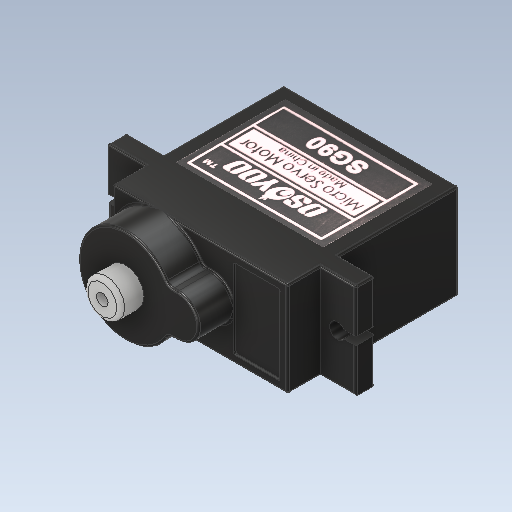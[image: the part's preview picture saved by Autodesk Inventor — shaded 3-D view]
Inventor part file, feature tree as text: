
AUTODESK INVENTOR PART (.ipt)
format: ipt  version: 2020 (Build 240168000, 168)  size: 1,720,320 bytes
history: native  units: mm
features: sketch x13, fillet x13, extrude x10, other x4, plane x1, projected_geometry x1
ambient origin geometry x8: Origin, YZ Plane, XZ Plane, XY Plane, X Axis, Y Axis, Z Axis, Center Point
bodies: Solid1 (feature_tree), Solid2 (feature_tree), Solid3 (feature_tree), Solid4 (feature_tree), Solid5 (feature_tree)
feature tree (42):
  extrude  "Extrusion1"  Depth=12.3mm
  plane  "Work Plane1"
  sketch  "Sketch2"  dims[d2=22.1mm d3=0.0mm d4=-6.6mm]
  extrude  "Extrusion2"  [1 undecoded]
  extrude  "Extrusion3"  Depth=2.4mm TaperAngle=0.0deg
  extrude  "Extrusion4"  Depth=2.0mm
  extrude  "Extrusion5"  Depth=1.0mm
  extrude  "Extrusion6"  Depth=2.4mm TaperAngle=0.0deg
  fillet  "Fillet1"  Radius=6.0mm
  extrude  "Extrusion7"  Depth=0.25mm TaperAngle=0.0deg
  fillet  "Fillet2"  Radius=4.5mm
  fillet  "Fillet3"  Radius=1.0mm
  fillet  "Fillet4"  Radius=4.8mm
  fillet  "Fillet5"  Radius=1.5mm
  fillet  "Fillet6"  Radius=3.0mm
  fillet  "Fillet7"  Radius=0.5mm
  fillet  "Fillet8"  Radius=0.25mm
  fillet  "Fillet9"  Radius=0.25mm
  fillet  "Fillet10"  Radius=0.25mm
  fillet  "Fillet11"  Radius=0.25mm
  fillet  "Fillet12"  Radius=0.25mm
  extrude  "Extrusion8"  Depth=0.25mm
  extrude  "Extrusion9"  Depth=0.25mm
  extrude  "Extrusion10"  Depth=3.0mm
  fillet  "Fillet13"  Radius=3.0mm
  other  "Decal1"
  other  "Decal2"
  sketch  "Sketch1"  dims[d0=22.6mm d1=12.3mm]
  sketch  "Sketch3"  dims[d5=32.0mm d6=2.4mm d7=0.0mm]
  sketch  "Sketch4"  dims[d8=2.0mm d9=2.0mm]
  sketch  "Sketch5"  dims[d10=1.0mm d11=1.0mm]
  projected_geometry  "Projected Loop1"
  sketch  "Sketch6"  dims[d12=2.4mm d13=0.0mm d14=4.5mm d15=0.0mm d16=6.0mm]
  sketch  "Sketch7"  dims[d17=10.3mm d18=0.3mm d19=0.0mm d20=4.5mm d21=0.0mm d22=1.0mm d23=4.8mm d24=1.5mm d25=3.0mm d26=0.0mm d27=0.5mm d28=0.25mm d29=0.25mm d30=0.25mm d31=0.25mm d32=0.25mm]
  sketch  "Sketch8"  dims[d33=0.25mm d34=0.25mm]
  sketch  "Sketch9"  dims[d35=0.25mm d36=0.25mm]
  sketch  "Sketch10"  dims[d37=0.25mm d38=1.0mm d39=3.0mm d40=0.0mm]
  sketch  "Sketch11"  dims[d41=1.0mm]
  sketch  "Sketch12"  dims[d42=3.0mm d43=0.0mm]
  other  "Image1"
  sketch  "Sketch13"  dims[d44=1.0mm d45=3.0mm d46=0.0mm d47=0.25mm]
  other  "Image2"
note: 1 required parameter value undecoded (feature->parameter linkage not recoverable at this tier; creation-order binding heuristic only, values carry confidence <= 0.55)
